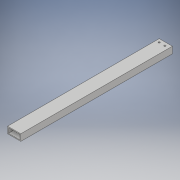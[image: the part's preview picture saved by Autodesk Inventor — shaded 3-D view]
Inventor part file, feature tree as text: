
AUTODESK INVENTOR PART (.ipt)
format: ipt  version: 2017 (Build 210142000, 142)  size: 118,784 bytes
history: native  units: in
note: dims shown in document units (in); Inventor stores cm internally (conversion verified against a paired STEP export)
features: sketch x2, extrude x1, hole x1
ambient origin geometry x8: Origin, YZ Plane, XZ Plane, XY Plane, X Axis, Y Axis, Z Axis, Center Point
bodies: Solid1 (feature_tree)
feature tree (4):
  extrude  "Extrusion1"  Depth=1.0in
  hole  "Hole1"  [1 undecoded]
  sketch  "Sketch1"  dims[d0=2.0in d1=1.0in]
  sketch  "Sketch2"  dims[d2=1.75in d3=0.75in d4=0.125in d5=0.125in d6=23.0in d7=0.0in d8=0.25in d9=90.0deg d10=0.5in d11=0.5in d12=12.25in d13=0.25in d14=0.75in d15=0.375in d16=0.25in d17=0.5635in d18=1.0in d19=0.8108in]
note: 1 required parameter value undecoded (feature->parameter linkage not recoverable at this tier; creation-order binding heuristic only, values carry confidence <= 0.55)
